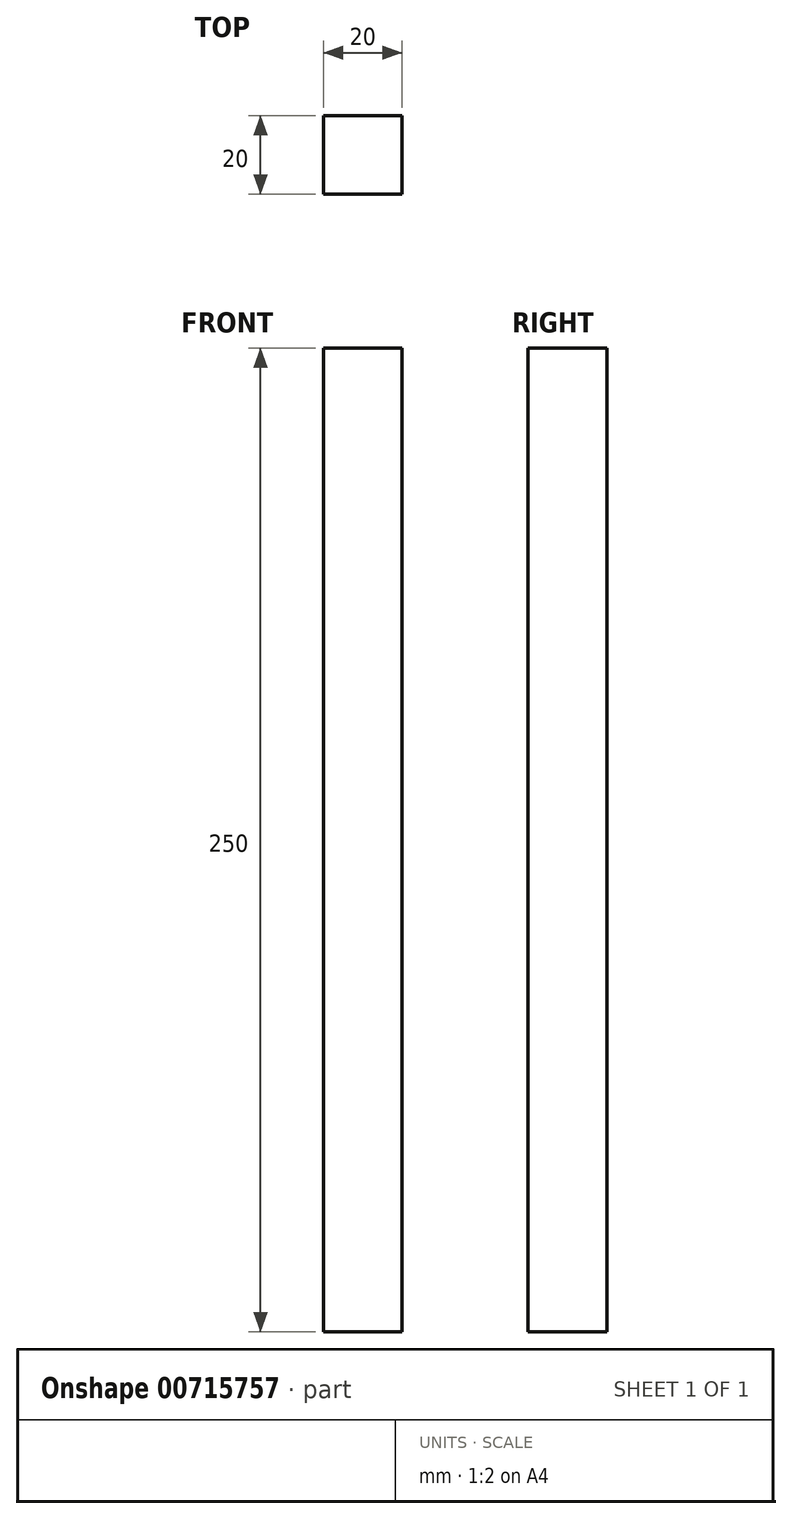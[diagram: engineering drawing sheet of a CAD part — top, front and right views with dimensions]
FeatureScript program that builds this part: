
annotation { "Feature Type Name" : "Feature", "Feature Type Description" : "" }
export const myFeature = defineFeature(function(context is Context, id is Id, definition is map)
    precondition{}
    {
        {
            var Q0;
            Q0=qCreatedBy(makeId("Top.planeOp"),FACE);
            var sketch = newSketch(context, id + "F0", { "sketchPlane" : qUnion([Q0])});
            skLineSegment(sketch, "E0.bottom", {"start": v(-10, 10) * mm, "end": v(10, 10) * mm});
            skLineSegment(sketch, "E0.top", {"start": v(-10, -10) * mm, "end": v(10, -10) * mm});
            skLineSegment(sketch, "E0.left", {"start": v(-10, 10) * mm, "end": v(-10, -10) * mm});
            skLineSegment(sketch, "E0.right", {"start": v(10, 10) * mm, "end": v(10, -10) * mm});
            skSolve(sketch);
        }
        {
            var Q0;
            Q0 = qSketchRegion(id + "F0", true);
            extrude(context, id + "F1", {"entities" : qUnion([Q0]), "depth" : 250 * mm, "offsetDistance" : 25 * mm});
        }
    });
